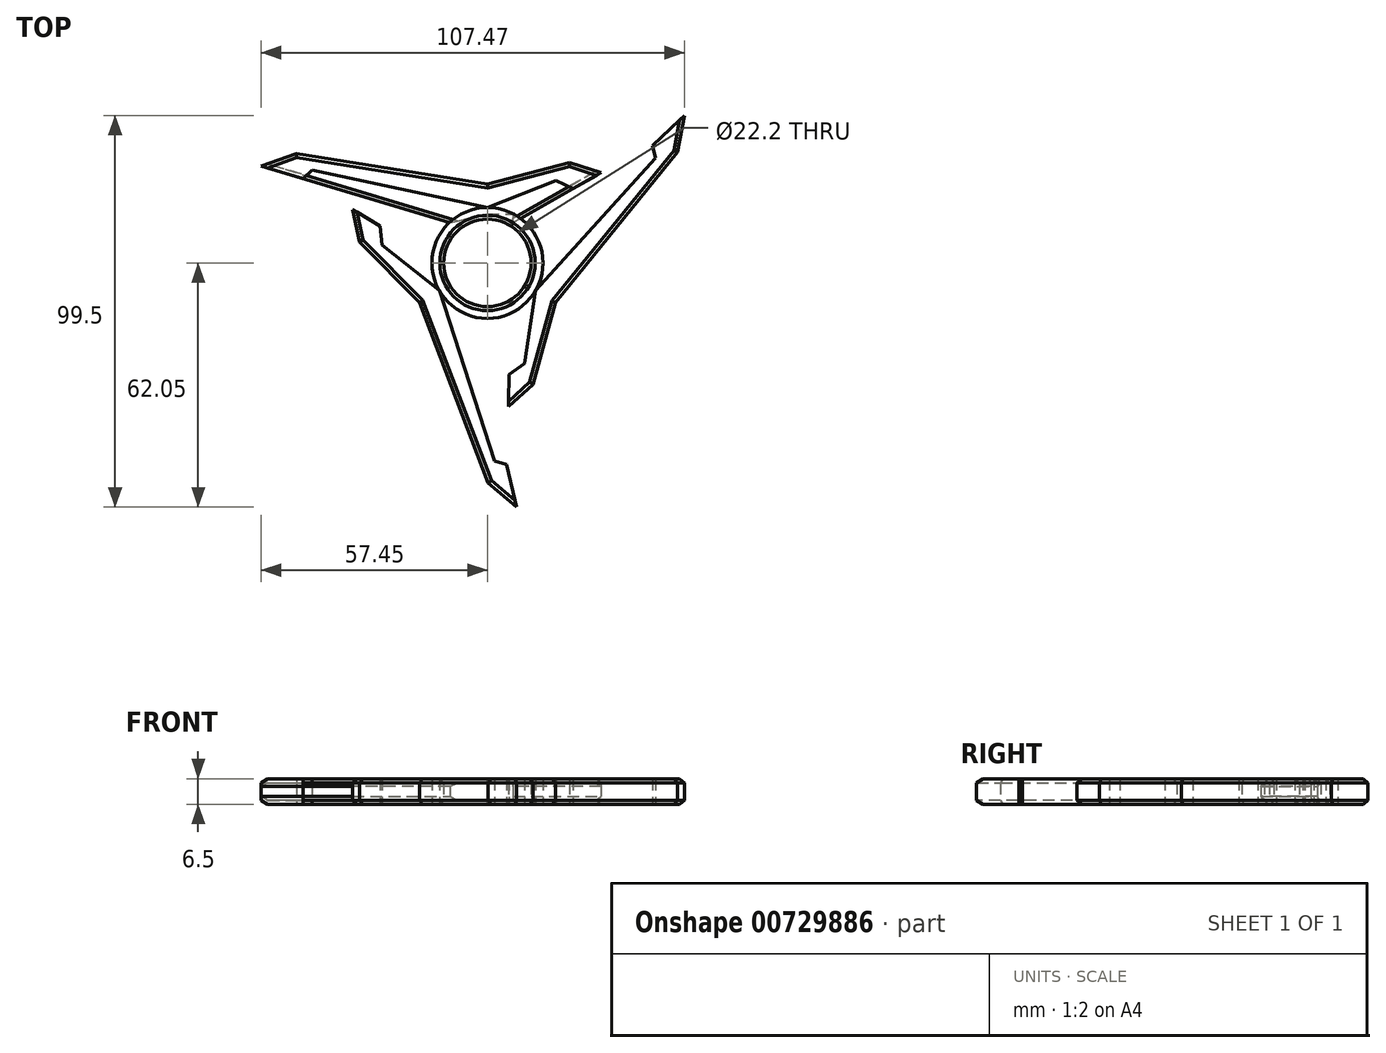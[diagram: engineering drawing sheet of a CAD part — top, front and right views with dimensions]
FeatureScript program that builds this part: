
annotation { "Feature Type Name" : "Feature", "Feature Type Description" : "" }
export const myFeature = defineFeature(function(context is Context, id is Id, definition is map)
    precondition{}
    {
        {
            var Q0;
            Q0=qCreatedBy(makeId("Top.planeOp"),FACE);
            var sketch = newSketch(context, id + "F0", { "sketchPlane" : qUnion([Q0])});
            skCircle(sketch, "E0", {"center": v(0, 0) * mm, "radius": 11.1 * mm});
            skCircle(sketch, "E1.0", {"center": v(0, 0) * mm, "radius": 14.1 * mm});
            skSolve(sketch);
        }
        {
            var Q0;
            Q0=qSketchRegion(id+"F0",true);
            extrude(context, id + "F1", {"entities" : qUnion([Q0]), "depth" : 6.5 * mm, "offsetDistance" : 25 * mm});
        }
        {
            var Q0;
            Q0=qCreatedBy(makeId("Front.planeOp"),FACE);
            var sketch = newSketch(context, id + "F2", { "sketchPlane" : qUnion([Q0])});
            skLineSegment(sketch, "E2", {"start": v(0, 0) * mm, "end": v(0, 20.18) * mm});
            skSolve(sketch);
        }
        {
            var Q0;
            Q0=qCreatedBy(makeId("Top.planeOp"),FACE);
            cPlane(context, id + "F3", {"entities" : qUnion([Q0]), "cplaneType" : CPlaneType.OFFSET, "offset" : 1 * mm, "width" : 150 * mm, "height" : 150 * mm});
        }
        {
            var Q0;
            Q0=qCreatedBy(id+"F3.planeOp",FACE);
            var sketch = newSketch(context, id + "F4", { "sketchPlane" : qUnion([Q0])});
            skLineSegment(sketch, "E3", {"start": v(0, 12.43) * mm, "end": v(6.5, 12.43) * mm});
            skLineSegment(sketch, "E4", {"start": v(6.5, 12.43) * mm, "end": v(6.5, 10.23) * mm});
            skLineSegment(sketch, "E5", {"start": v(-9.55, 10.23) * mm, "end": v(0, 12.43) * mm});
            skLineSegment(sketch, "E6", {"start": v(6.5, 10.23) * mm, "end": v(28.91, 22.93) * mm});
            skLineSegment(sketch, "E7", {"start": v(-9.55, 10.23) * mm, "end": v(-57.45, 24.6) * mm});
            skLineSegment(sketch, "E8", {"start": v(-57.45, 24.6) * mm, "end": v(-48.52, 27.8) * mm});
            skLineSegment(sketch, "E9", {"start": v(-48.52, 27.8) * mm, "end": v(0, 19.99) * mm});
            skLineSegment(sketch, "E10", {"start": v(0, 19.99) * mm, "end": v(20.91, 25.48) * mm});
            skLineSegment(sketch, "E11", {"start": v(20.91, 25.48) * mm, "end": v(28.91, 22.93) * mm});
            skLineSegment(sketch, "E12", {"start": v(0, 12.43) * mm, "end": v(0, 0) * mm});
            skLineSegment(sketch, "E13", {"start": v(0, 12.43) * mm, "end": v(0, 19.99) * mm});
            skSolve(sketch);
        }
        {
            var Q0;
            Q0=makeQuery(id+"F4.imprint","IMPRINT",FACE,{"disambiguationData":[TD([[makeQuery(id+"F4.imprint","IMPRINT",EDGE,{"derivedFrom":sQuery(id+"F4.wireOp",EDGE,"E3")}),1.0]])]});
            var Q1;
            Q1=makeQuery(id+"F4.imprint","IMPRINT",FACE,{"disambiguationData":[TD([[makeQuery(id+"F4.imprint","IMPRINT",EDGE,{"derivedFrom":sQuery(id+"F4.wireOp",EDGE,"E5")}),1.0]])]});
            extrude(context, id + "F5", {"entities" : qUnion([Q0, Q1]), "depth" : 4.5 * mm, "offsetDistance" : 25 * mm});
        }
        {
            var Q0;
            Q0=qCreatedBy(id+"F3.planeOp",FACE);
            cPlane(context, id + "F6", {"entities" : qUnion([Q0]), "cplaneType" : CPlaneType.OFFSET, "offset" : 1 * mm, "oppositeDirection" : true, "width" : 150 * mm, "height" : 150 * mm});
        }
        {
            var Q0;
            Q0=qCreatedBy(id+"F6.planeOp",FACE);
            var sketch = newSketch(context, id + "F7", { "sketchPlane" : qUnion([Q0])});
            skLineSegment(sketch, "E14", {"start": v(0, 12.43) * mm, "end": v(6.5, 12.43) * mm});
            skLineSegment(sketch, "E15", {"start": v(6.5, 12.43) * mm, "end": v(6.5, 10.23) * mm});
            skLineSegment(sketch, "E16", {"start": v(-9.55, 10.23) * mm, "end": v(0, 12.43) * mm});
            skLineSegment(sketch, "E17", {"start": v(6.5, 10.23) * mm, "end": v(28.92, 22.93) * mm});
            skLineSegment(sketch, "E18", {"start": v(-9.55, 10.23) * mm, "end": v(-57.45, 24.6) * mm});
            skLineSegment(sketch, "E19", {"start": v(-57.45, 24.6) * mm, "end": v(-48.52, 27.8) * mm});
            skLineSegment(sketch, "E20", {"start": v(-48.52, 27.8) * mm, "end": v(0, 19.99) * mm});
            skLineSegment(sketch, "E21", {"start": v(0, 19.99) * mm, "end": v(20.91, 25.48) * mm});
            skLineSegment(sketch, "E22", {"start": v(20.91, 25.48) * mm, "end": v(28.92, 22.93) * mm});
            skLineSegment(sketch, "E23", {"start": v(0, 12.43) * mm, "end": v(0, 0) * mm});
            skLineSegment(sketch, "E24", {"start": v(21.8, 18.9) * mm, "end": v(17.4, 20.93) * mm});
            skLineSegment(sketch, "E25", {"start": v(17.4, 20.93) * mm, "end": v(0, 14.1) * mm});
            skLineSegment(sketch, "E26", {"start": v(0, 14.1) * mm, "end": v(-47.96, 24.4) * mm});
            skLineSegment(sketch, "E27", {"start": v(-47.96, 24.4) * mm, "end": v(-50.42, 22.48) * mm});
            skLineSegment(sketch, "E28", {"start": v(0, 19.99) * mm, "end": v(0, 14.1) * mm});
            skLineSegment(sketch, "E29", {"start": v(0, 14.1) * mm, "end": v(0, 12.43) * mm});
            skLineSegment(sketch, "E30", {"start": v(-46.8, 21.4) * mm, "end": v(-44.49, 23.66) * mm});
            skSolve(sketch);
        }
        {
            var Q0;
            {var subQ0=sQuery(id+"F7.wireOp",EDGE,"E19");Q0=makeQuery(id+"F7.imprint","IMPRINT",FACE,{"disambiguationData":[TD([[makeQuery(id+"F7.imprint","IMPRINT",EDGE,{"derivedFrom":subQ0}),-1.0]])]});}
            var Q1;
            Q1=makeQuery(id+"F7.imprint","IMPRINT",FACE,{"disambiguationData":[TD([[makeQuery(id+"F7.imprint","IMPRINT",EDGE,{"derivedFrom":sQuery(id+"F7.wireOp",EDGE,"E21")}),-1.0]])]});
            var Q2;
            {var subQ0=sQuery(id+"F7.wireOp",EDGE,"E27");Q2=makeQuery(id+"F7.imprint","IMPRINT",FACE,{"disambiguationData":[TD([[makeQuery(id+"F7.imprint","IMPRINT",EDGE,{"derivedFrom":subQ0}),1.0]])]});}
            extrude(context, id + "F8", {"entities" : qUnion([Q0, Q1, Q2]), "depth" : 6.5 * mm, "offsetDistance" : 25 * mm});
        }
        {
            var Q0;
            Q0=makeQuery(id+"F8.opExtrude","CAP_EDGE",EDGE,{"disambiguationData":[OSD([sQuery(id+"F7.wireOp",EDGE,"E20")])],"isStart":false});
            var Q1;
            Q1=makeQuery(id+"F8.opExtrude","CAP_EDGE",EDGE,{"disambiguationData":[OSD([sQuery(id+"F7.wireOp",EDGE,"E21")])],"isStart":false});
            var Q2;
            Q2=makeQuery(id+"F8.opExtrude","CAP_EDGE",EDGE,{"disambiguationData":[OSD([sQuery(id+"F7.wireOp",EDGE,"E22")])],"isStart":false});
            var Q3;
            Q3=makeQuery(id+"F8.opExtrude","CAP_EDGE",EDGE,{"disambiguationData":[OSD([sQuery(id+"F7.wireOp",EDGE,"E19")])],"isStart":false});
            var Q4;
            Q4=makeQuery(id+"F8.opExtrude","CAP_EDGE",EDGE,{"disambiguationData":[OSD([sQuery(id+"F7.wireOp",EDGE,"E22")])],"isStart":true});
            var Q5;
            Q5=makeQuery(id+"F8.opExtrude","CAP_EDGE",EDGE,{"disambiguationData":[OSD([sQuery(id+"F7.wireOp",EDGE,"E21")])],"isStart":true});
            var Q6;
            Q6=makeQuery(id+"F8.opExtrude","CAP_EDGE",EDGE,{"disambiguationData":[OSD([sQuery(id+"F7.wireOp",EDGE,"E20")])],"isStart":true});
            var Q7;
            Q7=makeQuery(id+"F8.opExtrude","CAP_EDGE",EDGE,{"disambiguationData":[OSD([sQuery(id+"F7.wireOp",EDGE,"E19")])],"isStart":true});
            var Q8;
            Q8=makeQuery(id+"F5.opExtrude","CAP_EDGE",EDGE,{"disambiguationData":[OSD([sQuery(id+"F4.wireOp",EDGE,"E7")])],"isStart":false});
            var Q9;
            Q9=makeQuery(id+"F5.opExtrude","CAP_EDGE",EDGE,{"disambiguationData":[OSD([sQuery(id+"F4.wireOp",EDGE,"E7")])],"isStart":true});
            var Q10;
            Q10=makeQuery(id+"F5.opExtrude","CAP_EDGE",EDGE,{"disambiguationData":[OSD([sQuery(id+"F4.wireOp",EDGE,"E6")])],"isStart":true});
            var Q11;
            Q11=makeQuery(id+"F5.opExtrude","CAP_EDGE",EDGE,{"disambiguationData":[OSD([sQuery(id+"F4.wireOp",EDGE,"E6")])],"isStart":false});
            chamfer(context, id + "F9", {"entities" : qUnion([Q0, Q1, Q2, Q3, Q4, Q5, Q6, Q7, Q8, Q9, Q10, Q11]), "width" : 1 * mm, "tangentPropagation" : true});
        }
        {
            var Q0;
            Q0=makeQuery(id+"F8.opExtrude","SWEPT_BODY",BODY,{"disambiguationData":[OSD([sQuery(id+"F7.wireOp",EDGE,"E17"),sQuery(id+"F7.wireOp",EDGE,"E18"),sQuery(id+"F7.wireOp",EDGE,"E19"),sQuery(id+"F7.wireOp",EDGE,"E20"),sQuery(id+"F7.wireOp",EDGE,"E21"),sQuery(id+"F7.wireOp",EDGE,"E22"),sQuery(id+"F7.wireOp",EDGE,"E24"),sQuery(id+"F7.wireOp",EDGE,"E25"),sQuery(id+"F7.wireOp",EDGE,"E26"),sQuery(id+"F7.wireOp",EDGE,"E27")])]});
            var Q1;
            Q1=makeQuery(id+"F1.opExtrude","SWEPT_FACE",FACE,{"disambiguationData":[OSD([sQuery(id+"F0.wireOp",EDGE,"E1.0")])]});
            circularPattern(context, id + "F10", {"entities" : qUnion([Q0]), "axis" : qUnion([Q1]), "angle" : 360 * degree, "instanceCount" : 3, "equalSpace" : true});
        }
        {
            var Q0;
            Q0=makeQuery(id+"F1.opExtrude","CAP_EDGE",EDGE,{"disambiguationData":[OSD([sQuery(id+"F0.wireOp",EDGE,"E0")])],"isStart":false});
            var Q1;
            Q1=makeQuery(id+"F1.opExtrude","SWEPT_FACE",FACE,{"disambiguationData":[OSD([sQuery(id+"F0.wireOp",EDGE,"E0")])]});
            chamfer(context, id + "F11", {"entities" : qUnion([Q0, Q1]), "width" : 1 * mm, "tangentPropagation" : true});
        }
    });
